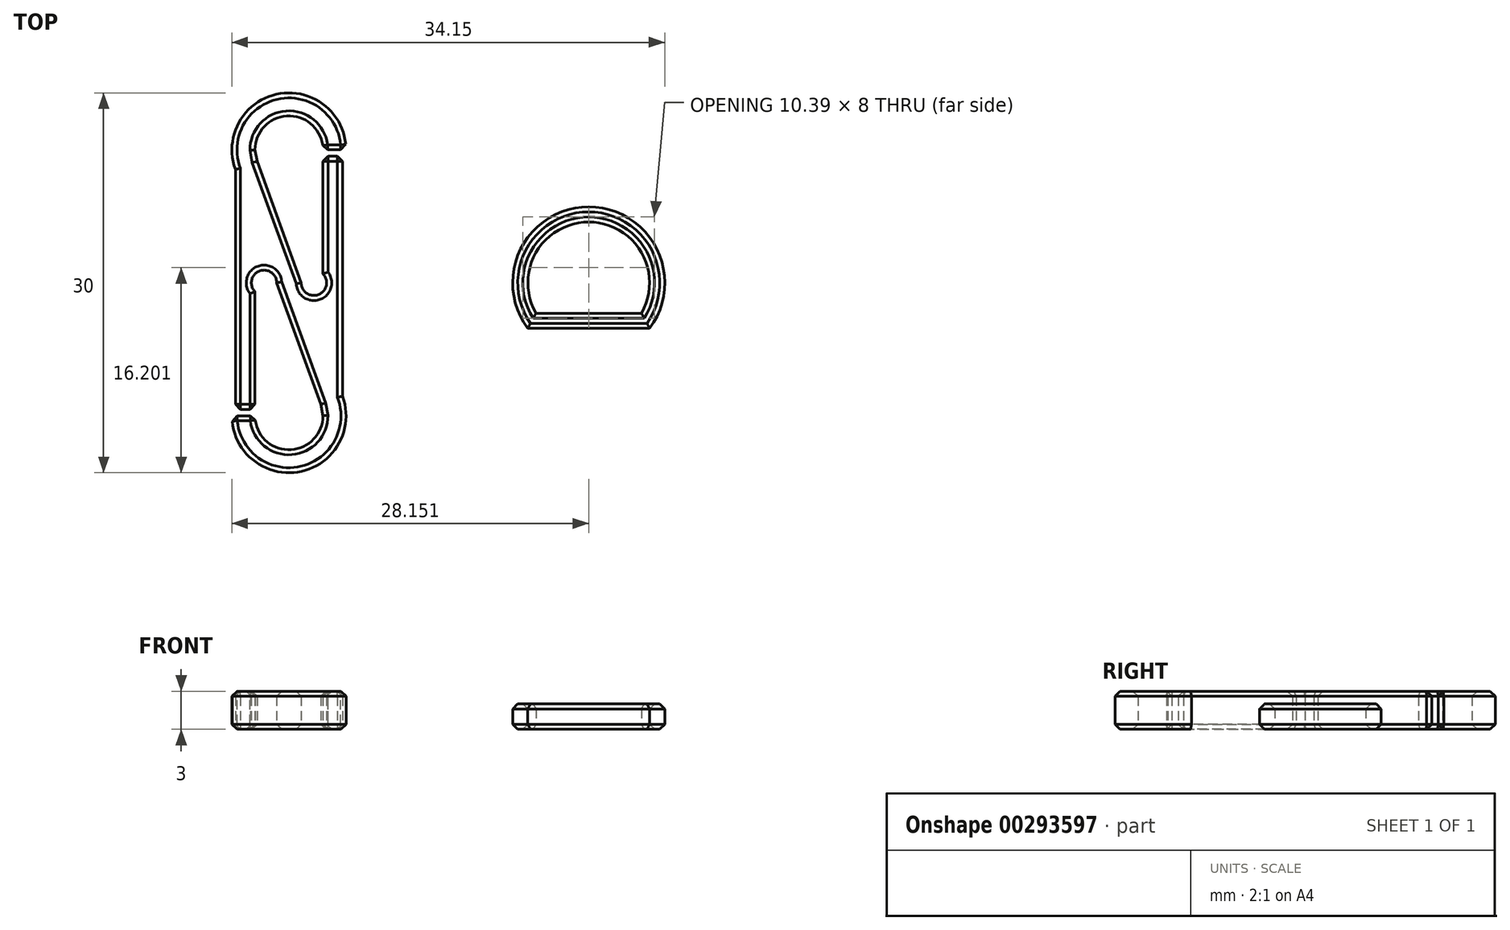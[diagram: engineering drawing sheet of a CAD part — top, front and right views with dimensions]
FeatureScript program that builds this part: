
annotation { "Feature Type Name" : "Feature", "Feature Type Description" : "" }
export const myFeature = defineFeature(function(context is Context, id is Id, definition is map)
    precondition{}
    {
        {
            var Q0;
            Q0=qCreatedBy(makeId("Top.planeOp"),FACE);
            var sketch = newSketch(context, id + "F0", { "sketchPlane" : qUnion([Q0])});
            skArc(sketch, "E0", {"start": v(4.5, 0) * mm, "mid": v(-0.78, 4.43) * mm, "end": v(-4.23, -1.54) * mm});
            skArc(sketch, "E1", {"start": v(-4.5, -21) * mm, "mid": v(0.78, -25.43) * mm, "end": v(4.23, -19.46) * mm});
            skArc(sketch, "E2", {"start": v(2.68, 0) * mm, "mid": v(0, 2.68) * mm, "end": v(-2.68, 0) * mm});
            skArc(sketch, "E3", {"start": v(-2.68, -21) * mm, "mid": v(0, -23.68) * mm, "end": v(2.68, -21) * mm});
            skLineSegment(sketch, "E4", {"start": v(-4.5, 0) * mm, "end": v(4.5, 0) * mm, "construction": true});
            skLineSegment(sketch, "E5", {"start": v(-4.5, -21) * mm, "end": v(4.5, -21) * mm, "construction": true});
            skPoint(sketch, "E6", {"position": v(-2.68, 0) * mm});
            skPoint(sketch, "E7", {"position": v(2.68, 0) * mm});
            skPoint(sketch, "E8", {"position": v(2.68, -21) * mm});
            skPoint(sketch, "E9", {"position": v(-2.68, -21) * mm});
            skLineSegment(sketch, "E10", {"start": v(2.52, -20.08) * mm, "end": v(-0.97, -10.5) * mm});
            skLineSegment(sketch, "E11", {"start": v(4.23, -19.46) * mm, "end": v(1.2, -11.14) * mm, "construction": true});
            skPoint(sketch, "E12", {"position": v(0.86, -10.19) * mm});
            skPoint(sketch, "E13", {"position": v(-0.86, -10.81) * mm});
            skLineSegment(sketch, "E14", {"start": v(0, 0) * mm, "end": v(0, -21) * mm, "construction": true});
            skPoint(sketch, "E15", {"position": v(0, -10.5) * mm});
            skLineSegment(sketch, "E16", {"start": v(-8.34, -10.5) * mm, "end": v(-4.23, -10.5) * mm, "construction": true});
            skLineSegment(sketch, "E17", {"start": v(4.23, -19.46) * mm, "end": v(4.23, -10.5) * mm});
            skLineSegment(sketch, "E18", {"start": v(-4.23, -1.54) * mm, "end": v(-4.23, -10.5) * mm});
            skLineSegment(sketch, "E19", {"start": v(2.68, 0) * mm, "end": v(4.5, 0) * mm});
            skLineSegment(sketch, "E20", {"start": v(4.23, -10.5) * mm, "end": v(4.23, -0.5) * mm});
            skLineSegment(sketch, "E21", {"start": v(4.23, -0.5) * mm, "end": v(2.68, -0.5) * mm});
            skLineSegment(sketch, "E22", {"start": v(2.68, -0.5) * mm, "end": v(2.68, -9.8) * mm});
            skLineSegment(sketch, "E23", {"start": v(-4.23, -10.5) * mm, "end": v(-4.23, -20.5) * mm});
            skLineSegment(sketch, "E24", {"start": v(-4.23, -20.5) * mm, "end": v(-2.68, -20.5) * mm});
            skLineSegment(sketch, "E25", {"start": v(-2.68, -20.5) * mm, "end": v(-2.68, -11.2) * mm});
            skLineSegment(sketch, "E26", {"start": v(-4.5, -21) * mm, "end": v(-2.68, -21) * mm});
            skLineSegment(sketch, "E27", {"start": v(2.52, -20.08) * mm, "end": v(2.68, -21) * mm});
            skLineSegment(sketch, "E28", {"start": v(-2.52, -0.92) * mm, "end": v(-2.68, 0) * mm});
            skCircle(sketch, "E29", {"center": v(-1.97, -10.5) * mm, "radius": 1 * mm});
            skCircle(sketch, "E30.MirrorC", {"center": v(1.97, -10.5) * mm, "radius": 1 * mm});
            skPoint(sketch, "E31.orphan", {"position": v(-2.68, -10.5) * mm});
            skLineSegment(sketch, "E32.trimOffspring", {"start": v(-0.97, -10.5) * mm, "end": v(0.97, -10.5) * mm, "construction": true});
            skLineSegment(sketch, "E33.trimOffspring", {"start": v(-1.2, -9.86) * mm, "end": v(-4.23, -1.54) * mm, "construction": true});
            skLineSegment(sketch, "E34.trimOffspring", {"start": v(0.97, -10.5) * mm, "end": v(-2.52, -0.92) * mm});
            skLineSegment(sketch, "E35.trimOffspring", {"start": v(4.23, -10.5) * mm, "end": v(7.38, -10.5) * mm, "construction": true});
            skPoint(sketch, "E36.orphan", {"position": v(2.68, -10.5) * mm});
            skArc(sketch, "E37", {"start": v(28.45, -14.1) * mm, "mid": v(23.65, -4.5) * mm, "end": v(18.85, -14.1) * mm});
            skArc(sketch, "E38", {"start": v(27.8, -12.9) * mm, "mid": v(23.65, -5.7) * mm, "end": v(19.5, -12.9) * mm});
            skLineSegment(sketch, "E39", {"start": v(23.65, -4.5) * mm, "end": v(23.65, -14.1) * mm, "construction": true});
            skLineSegment(sketch, "E40", {"start": v(23.65, -10.5) * mm, "end": v(18.15, -12.9) * mm, "construction": true});
            skLineSegment(sketch, "E41.MirrorCS", {"start": v(23.65, -10.5) * mm, "end": v(29.15, -12.9) * mm, "construction": true});
            skLineSegment(sketch, "E42", {"start": v(18.15, -12.9) * mm, "end": v(29.15, -12.9) * mm, "construction": true});
            skLineSegment(sketch, "E43", {"start": v(18.85, -14.1) * mm, "end": v(28.45, -14.1) * mm});
            skLineSegment(sketch, "E44", {"start": v(19.5, -12.9) * mm, "end": v(27.8, -12.9) * mm});
            skSolve(sketch);
        }
        {
            var Q0;
            Q0=makeQuery(id+"F0.imprint","IMPRINT",FACE,{"disambiguationData":[TD([[makeQuery(id+"F0.imprint","IMPRINT",EDGE,{"derivedFrom":sQuery(id+"F0.wireOp",EDGE,"E0")}),1.0]])]});
            extrude(context, id + "F1", {"entities" : qUnion([Q0]), "depth" : 3 * mm});
        }
        {
            var Q0;
            Q0=makeQuery(id+"F0.imprint","IMPRINT",FACE,{"disambiguationData":[TD([[makeQuery(id+"F0.imprint","IMPRINT",EDGE,{"derivedFrom":sQuery(id+"F0.wireOp",EDGE,"E37")}),1.0]])]});
            extrude(context, id + "F2", {"entities" : qUnion([Q0]), "depth" : 2 * mm});
        }
        {
            var Q0;
            Q0=makeQuery(id+"F1.opExtrude","SWEPT_FACE",FACE,{"disambiguationData":[OSD([sQuery(id+"F0.wireOp",EDGE,"E19")])]});
            var Q1;
            Q1=makeQuery(id+"F1.opExtrude","SWEPT_FACE",FACE,{"disambiguationData":[OSD([sQuery(id+"F0.wireOp",EDGE,"E21")])]});
            var Q2;
            Q2=makeQuery(id+"F1.opExtrude","SWEPT_FACE",FACE,{"disambiguationData":[OSD([sQuery(id+"F0.wireOp",EDGE,"E24")])]});
            var Q3;
            Q3=makeQuery(id+"F1.opExtrude","SWEPT_FACE",FACE,{"disambiguationData":[OSD([sQuery(id+"F0.wireOp",EDGE,"E26")])]});
            var Q4;
            Q4=makeQuery(id+"F1.opExtrude","CAP_FACE",FACE,{"disambiguationData":[OSD([sQuery(id+"F0.wireOp",EDGE,"E0"),sQuery(id+"F0.wireOp",EDGE,"E1"),sQuery(id+"F0.wireOp",EDGE,"E2"),sQuery(id+"F0.wireOp",EDGE,"E3"),sQuery(id+"F0.wireOp",EDGE,"E10"),sQuery(id+"F0.wireOp",EDGE,"E17"),sQuery(id+"F0.wireOp",EDGE,"E18"),sQuery(id+"F0.wireOp",EDGE,"E19"),sQuery(id+"F0.wireOp",EDGE,"E20"),sQuery(id+"F0.wireOp",EDGE,"E21"),sQuery(id+"F0.wireOp",EDGE,"E22"),sQuery(id+"F0.wireOp",EDGE,"E23"),sQuery(id+"F0.wireOp",EDGE,"E24"),sQuery(id+"F0.wireOp",EDGE,"E25"),sQuery(id+"F0.wireOp",EDGE,"E26"),sQuery(id+"F0.wireOp",EDGE,"E27"),sQuery(id+"F0.wireOp",EDGE,"E28"),sQuery(id+"F0.wireOp",EDGE,"E29"),sQuery(id+"F0.wireOp",EDGE,"E30.MirrorC"),sQuery(id+"F0.wireOp",EDGE,"E34.trimOffspring")])],"isStart":false});
            var Q5;
            Q5=makeQuery(id+"F1.opExtrude","CAP_FACE",FACE,{"disambiguationData":[OSD([sQuery(id+"F0.wireOp",EDGE,"E0"),sQuery(id+"F0.wireOp",EDGE,"E1"),sQuery(id+"F0.wireOp",EDGE,"E2"),sQuery(id+"F0.wireOp",EDGE,"E3"),sQuery(id+"F0.wireOp",EDGE,"E10"),sQuery(id+"F0.wireOp",EDGE,"E17"),sQuery(id+"F0.wireOp",EDGE,"E18"),sQuery(id+"F0.wireOp",EDGE,"E19"),sQuery(id+"F0.wireOp",EDGE,"E20"),sQuery(id+"F0.wireOp",EDGE,"E21"),sQuery(id+"F0.wireOp",EDGE,"E22"),sQuery(id+"F0.wireOp",EDGE,"E23"),sQuery(id+"F0.wireOp",EDGE,"E24"),sQuery(id+"F0.wireOp",EDGE,"E25"),sQuery(id+"F0.wireOp",EDGE,"E26"),sQuery(id+"F0.wireOp",EDGE,"E27"),sQuery(id+"F0.wireOp",EDGE,"E28"),sQuery(id+"F0.wireOp",EDGE,"E29"),sQuery(id+"F0.wireOp",EDGE,"E30.MirrorC"),sQuery(id+"F0.wireOp",EDGE,"E34.trimOffspring")])],"isStart":true});
            var Q6;
            Q6=makeQuery(id+"F2.opExtrude","CAP_FACE",FACE,{"disambiguationData":[OSD([sQuery(id+"F0.wireOp",EDGE,"E37"),sQuery(id+"F0.wireOp",EDGE,"E38"),sQuery(id+"F0.wireOp",EDGE,"E43"),sQuery(id+"F0.wireOp",EDGE,"E44")])],"isStart":false});
            var Q7;
            Q7=makeQuery(id+"F2.opExtrude","CAP_FACE",FACE,{"disambiguationData":[OSD([sQuery(id+"F0.wireOp",EDGE,"E37"),sQuery(id+"F0.wireOp",EDGE,"E38"),sQuery(id+"F0.wireOp",EDGE,"E43"),sQuery(id+"F0.wireOp",EDGE,"E44")])],"isStart":true});
            chamfer(context, id + "F3", {"entities" : qUnion([Q0, Q1, Q2, Q3, Q4, Q5, Q6, Q7]), "width" : 0.4 * mm, "tangentPropagation" : true});
        }
    });
